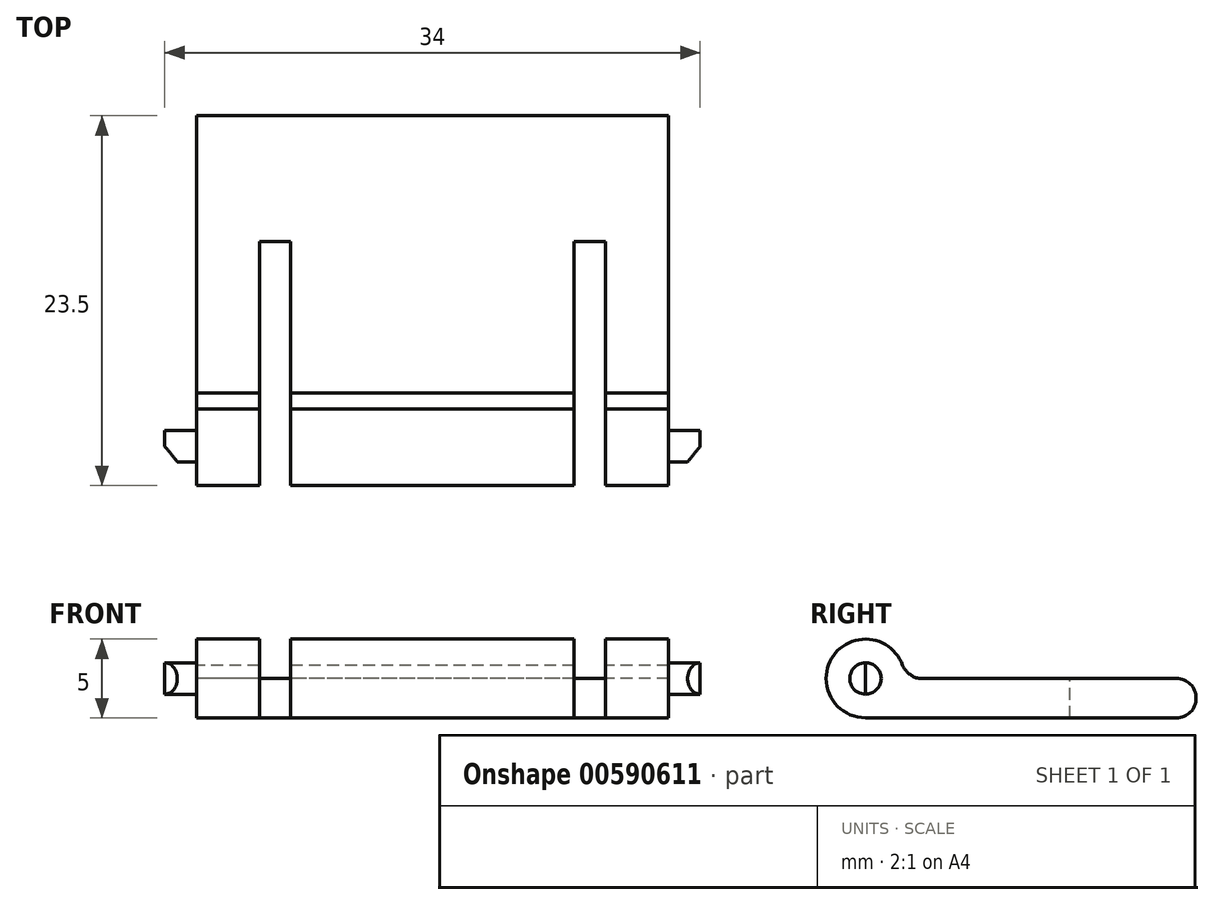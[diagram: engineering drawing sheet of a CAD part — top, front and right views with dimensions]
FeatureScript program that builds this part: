
annotation { "Feature Type Name" : "Feature", "Feature Type Description" : "" }
export const myFeature = defineFeature(function(context is Context, id is Id, definition is map)
    precondition{}
    {
        {
            var Q0;
            Q0=qCreatedBy(makeId("Right.planeOp"),FACE);
            var sketch = newSketch(context, id + "F0", { "sketchPlane" : qUnion([Q0])});
            skCircle(sketch, "E0", {"center": v(0, 0) * mm, "radius": 1 * mm});
            skCircle(sketch, "E1", {"center": v(0, 0) * mm, "radius": 2.5 * mm});
            skLineSegment(sketch, "E2.bottom", {"start": v(19.75, -2.5) * mm, "end": v(0, -2.5) * mm});
            skLineSegment(sketch, "E2.top", {"start": v(19.75, 0) * mm, "end": v(0, 0) * mm});
            skLineSegment(sketch, "E2.left", {"start": v(19.75, -2.5) * mm, "end": v(19.75, 0) * mm});
            skLineSegment(sketch, "E2.right", {"start": v(0, -2.5) * mm, "end": v(0, 0) * mm});
            skPoint(sketch, "E3", {"position": v(2.5, 0) * mm});
            skArc(sketch, "E4", {"start": v(2.3, 0.97) * mm, "mid": v(2.72, 0.34) * mm, "end": v(3.39, 0) * mm});
            skCircle(sketch, "E5", {"center": v(19.75, -1.25) * mm, "radius": 1.25 * mm});
            skPoint(sketch, "E5.first.point", {"position": v(19.75, 0) * mm});
            skPoint(sketch, "E5.second.point", {"position": v(21, -1.25) * mm});
            skPoint(sketch, "E5.third.point", {"position": v(19.75, -2.5) * mm});
            skSolve(sketch);
        }
        {
            var Q0;
            Q0 = qSketchRegion(id + "F0", true);
            extrude(context, id + "F1", {"entities" : qUnion([Q0]), "endBound" : BoundingType.SYMMETRIC, "depth" : 30 * mm, "offsetDistance" : 25 * mm});
        }
        {
            var Q0;
            Q0=qCreatedBy(makeId("Right.planeOp"),FACE);
            var sketch = newSketch(context, id + "F2", { "sketchPlane" : qUnion([Q0])});
            skCircle(sketch, "E6", {"center": v(0, 0) * mm, "radius": 1 * mm});
            skSolve(sketch);
        }
        {
            var Q0;
            Q0 = qSketchRegion(id + "F2", true);
            extrude(context, id + "F3", {"entities" : qUnion([Q0]), "operationType" : NewBodyOperationType.ADD, "endBound" : BoundingType.SYMMETRIC, "depth" : 34 * mm, "offsetDistance" : 25 * mm});
        }
        {
            var Q0;
            Q0=qCreatedBy(makeId("Top.planeOp"),FACE);
            var sketch = newSketch(context, id + "F4", { "sketchPlane" : qUnion([Q0])});
            skLineSegment(sketch, "E7", {"start": v(-17, 0) * mm, "end": v(-14.56, -3.04) * mm});
            skLineSegment(sketch, "E8", {"start": v(-14.56, -3.04) * mm, "end": v(-18.74, -3.04) * mm});
            skLineSegment(sketch, "E9", {"start": v(-18.74, -3.04) * mm, "end": v(-18.74, 0) * mm});
            skLineSegment(sketch, "E10", {"start": v(-18.74, 0) * mm, "end": v(-17, 0) * mm});
            skLineSegment(sketch, "E11.MirrorCS", {"start": v(18.74, 0) * mm, "end": v(17, 0) * mm});
            skLineSegment(sketch, "E12.MirrorCS", {"start": v(14.56, -3.04) * mm, "end": v(18.74, -3.04) * mm});
            skLineSegment(sketch, "E13.MirrorCS", {"start": v(17, 0) * mm, "end": v(14.56, -3.04) * mm});
            skLineSegment(sketch, "E14.MirrorCS", {"start": v(18.74, -3.04) * mm, "end": v(18.74, 0) * mm});
            skSolve(sketch);
        }
        {
            var Q0;
            Q0=qCreatedBy(makeId("Top.planeOp"),FACE);
            var sketch = newSketch(context, id + "F5", { "sketchPlane" : qUnion([Q0])});
            skLineSegment(sketch, "E15.bottom", {"start": v(-11, -5.86) * mm, "end": v(-9, -5.86) * mm});
            skLineSegment(sketch, "E15.top", {"start": v(-11, 13) * mm, "end": v(-9, 13) * mm});
            skLineSegment(sketch, "E15.left", {"start": v(-11, -5.86) * mm, "end": v(-11, 13) * mm});
            skLineSegment(sketch, "E15.right", {"start": v(-9, -5.86) * mm, "end": v(-9, 13) * mm});
            skLineSegment(sketch, "E16.MirrorCS", {"start": v(11, -5.86) * mm, "end": v(9, -5.86) * mm});
            skLineSegment(sketch, "E17.MirrorCS", {"start": v(11, 13) * mm, "end": v(9, 13) * mm});
            skLineSegment(sketch, "E18.MirrorCS", {"start": v(9, -5.86) * mm, "end": v(9, 13) * mm});
            skLineSegment(sketch, "E19.MirrorCS", {"start": v(11, -5.86) * mm, "end": v(11, 13) * mm});
            skSolve(sketch);
        }
        {
            var Q0;
            Q0 = qSketchRegion(id + "F4", true);
            var Q1;
            Q1=makeQuery(id+"F5.imprint","IMPRINT",FACE,{"disambiguationData":[TD([[makeQuery(id+"F5.imprint","IMPRINT",EDGE,{"derivedFrom":sQuery(id+"F5.wireOp",EDGE,"E15.bottom")}),1.0]])]});
            var Q2;
            Q2=makeQuery(id+"F5.imprint","IMPRINT",FACE,{"disambiguationData":[TD([[makeQuery(id+"F5.imprint","IMPRINT",EDGE,{"derivedFrom":sQuery(id+"F5.wireOp",EDGE,"E16.MirrorCS")}),-1.0]])]});
            extrude(context, id + "F6", {"entities" : qUnion([Q0, Q1, Q2]), "operationType" : NewBodyOperationType.REMOVE, "endBound" : BoundingType.SYMMETRIC, "oppositeDirection" : true, "depth" : 25 * mm, "offsetDistance" : 25 * mm});
        }
    });
